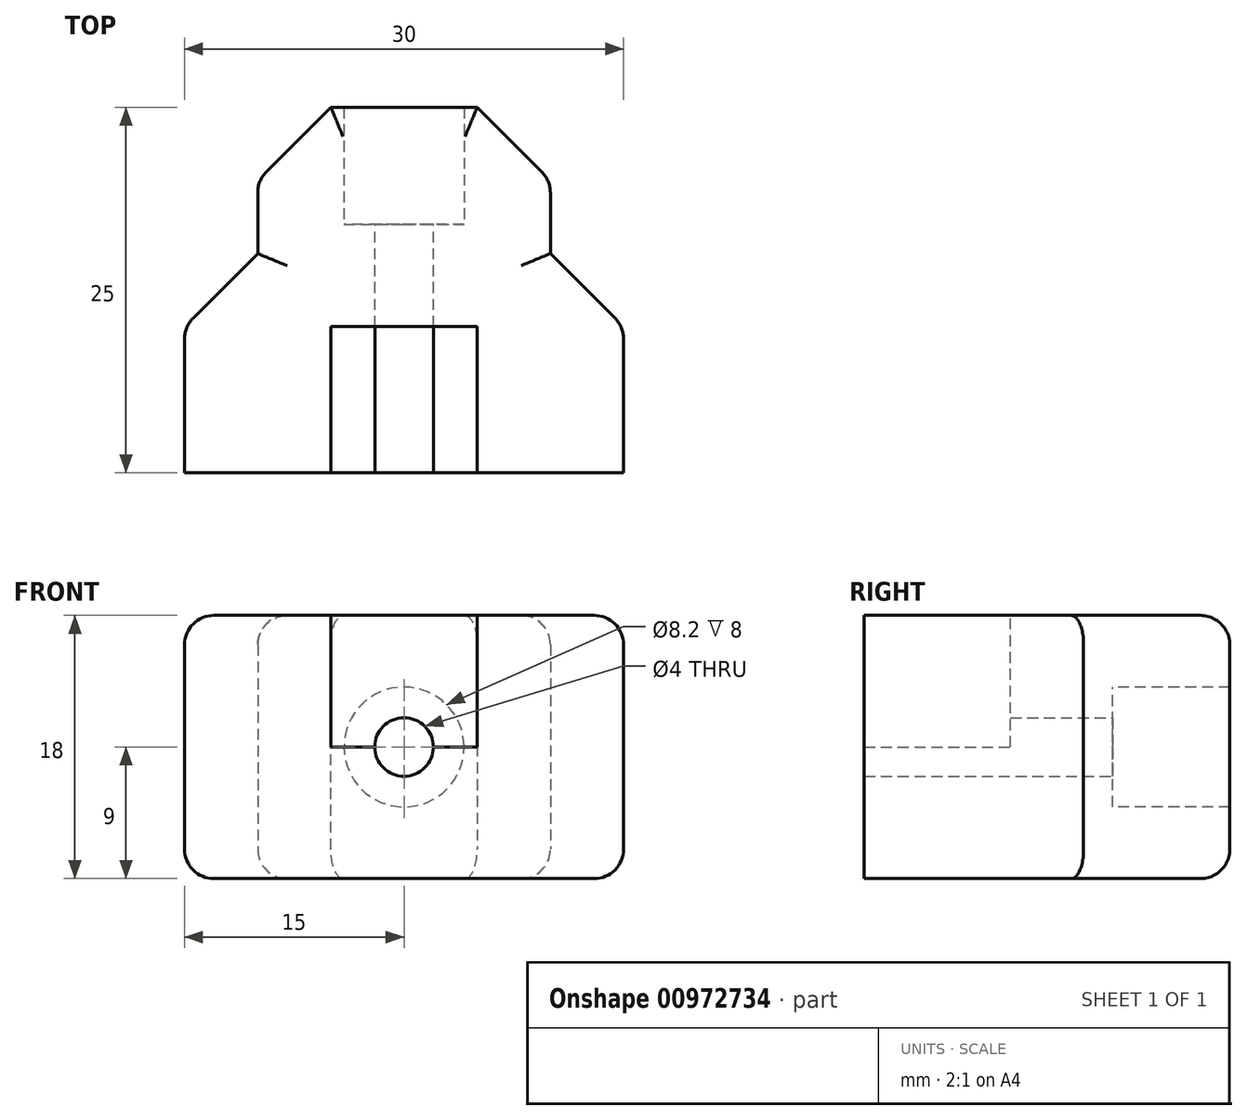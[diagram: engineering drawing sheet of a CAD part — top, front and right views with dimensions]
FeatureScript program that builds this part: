
annotation { "Feature Type Name" : "Feature", "Feature Type Description" : "" }
export const myFeature = defineFeature(function(context is Context, id is Id, definition is map)
    precondition{}
    {
        {
            var Q0;
            Q0=qCreatedBy(makeId("Front.planeOp"),FACE);
            var sketch = newSketch(context, id + "F0", { "sketchPlane" : qUnion([Q0])});
            skLineSegment(sketch, "E0.bottom", {"start": v(15, 9) * mm, "end": v(-15, 9) * mm});
            skLineSegment(sketch, "E0.top", {"start": v(15, -9) * mm, "end": v(-15, -9) * mm});
            skLineSegment(sketch, "E0.left", {"start": v(15, 9) * mm, "end": v(15, -9) * mm});
            skLineSegment(sketch, "E0.right", {"start": v(-15, 9) * mm, "end": v(-15, -9) * mm});
            skPoint(sketch, "E0.middle", {"position": v(0, 0) * mm});
            skLineSegment(sketch, "E1.bottom", {"start": v(10, 9) * mm, "end": v(-10, 9) * mm});
            skLineSegment(sketch, "E1.top", {"start": v(10, -9) * mm, "end": v(-10, -9) * mm});
            skLineSegment(sketch, "E1.left", {"start": v(10, 9) * mm, "end": v(10, -9) * mm});
            skLineSegment(sketch, "E1.right", {"start": v(-10, 9) * mm, "end": v(-10, -9) * mm});
            skCircle(sketch, "E2", {"center": v(0, 0) * mm, "radius": 4.1 * mm});
            skCircle(sketch, "E3", {"center": v(0, 0) * mm, "radius": 2 * mm});
            skLineSegment(sketch, "E4.bottom", {"start": v(-5, 0) * mm, "end": v(5, 0) * mm});
            skLineSegment(sketch, "E4.top", {"start": v(-5, 9) * mm, "end": v(5, 9) * mm});
            skLineSegment(sketch, "E4.left", {"start": v(-5, 0) * mm, "end": v(-5, 9) * mm});
            skLineSegment(sketch, "E4.right", {"start": v(5, 0) * mm, "end": v(5, 9) * mm});
            skSolve(sketch);
        }
        {
            var Q0;
            {var subQ0=sQuery(id+"F0.wireOp",EDGE,"E0.right");Q0=makeQuery(id+"F0.imprint","IMPRINT",FACE,{"disambiguationData":[TD([[makeQuery(id+"F0.imprint","IMPRINT",EDGE,{"derivedFrom":subQ0}),1.0]])]});}
            var Q1;
            {var subQ0=sQuery(id+"F0.wireOp",EDGE,"E1.left");Q1=makeQuery(id+"F0.imprint","IMPRINT",FACE,{"disambiguationData":[TD([[makeQuery(id+"F0.imprint","IMPRINT",EDGE,{"derivedFrom":subQ0}),-1.0]])]});}
            var Q2;
            {var subQ2=sQuery(id+"F0.wireOp",EDGE,"E0.left");Q2=makeQuery(id+"F0.imprint","IMPRINT",FACE,{"disambiguationData":[TD([[makeQuery(id+"F0.imprint","IMPRINT",EDGE,{"derivedFrom":subQ2}),-1.0]])]});}
            var Q3;
            {var subQ0=sQuery(id+"F0.wireOp",EDGE,"E4.bottom");var subQ1=sQuery(id+"F0.wireOp",EDGE,"E2");var subQ2=makeQuery(id+"F0.imprint","INTERSECT",VERTEX,{"disambiguationData":[OD(0.0)],"derivedFrom":[subQ1,subQ0]});Q3=makeQuery(id+"F0.imprint","IMPRINT",FACE,{"disambiguationData":[TD([[makeQuery(id+"F0.imprint","IMPRINT",EDGE,{"disambiguationData":[TD([[subQ2,-1.0]])],"derivedFrom":subQ1}),1.0]])]});}
            extrude(context, id + "F1", {"entities" : qUnion([Q0, Q1, Q2, Q3]), "depth" : 15 * mm, "offsetDistance" : 25 * mm});
        }
        {
            var Q0;
            {var subQ5=sQuery(id+"F0.wireOp",EDGE,"E4.left");Q0=makeQuery(id+"F0.imprint","IMPRINT",FACE,{"disambiguationData":[TD([[makeQuery(id+"F0.imprint","IMPRINT",EDGE,{"derivedFrom":subQ5}),-1.0]])]});}
            var Q1;
            {var subQ0=sQuery(id+"F0.wireOp",EDGE,"E4.bottom");var subQ1=sQuery(id+"F0.wireOp",EDGE,"E2");var subQ2=makeQuery(id+"F0.imprint","INTERSECT",VERTEX,{"disambiguationData":[OD(0.0)],"derivedFrom":[subQ1,subQ0]});Q1=makeQuery(id+"F0.imprint","IMPRINT",FACE,{"disambiguationData":[TD([[makeQuery(id+"F0.imprint","IMPRINT",EDGE,{"disambiguationData":[TD([[subQ2,1.0]])],"derivedFrom":subQ1}),1.0]])]});}
            extrude(context, id + "F2", {"entities" : qUnion([Q0, Q1]), "operationType" : NewBodyOperationType.ADD, "depth" : 5 * mm, "offsetDistance" : 25 * mm});
        }
        {
            var Q0;
            {var subQ0=sQuery(id+"F0.wireOp",EDGE,"E1.left");Q0=makeQuery(id+"F0.imprint","IMPRINT",FACE,{"disambiguationData":[TD([[makeQuery(id+"F0.imprint","IMPRINT",EDGE,{"derivedFrom":subQ0}),-1.0]])]});}
            var Q1;
            {var subQ5=sQuery(id+"F0.wireOp",EDGE,"E4.left");Q1=makeQuery(id+"F0.imprint","IMPRINT",FACE,{"disambiguationData":[TD([[makeQuery(id+"F0.imprint","IMPRINT",EDGE,{"derivedFrom":subQ5}),-1.0]])]});}
            extrude(context, id + "F3", {"entities" : qUnion([Q0, Q1]), "operationType" : NewBodyOperationType.ADD, "oppositeDirection" : true, "depth" : 10 * mm, "offsetDistance" : 25 * mm});
        }
        {
            var Q0;
            {var subQ0=sQuery(id+"F0.wireOp",EDGE,"E4.bottom");var subQ1=sQuery(id+"F0.wireOp",EDGE,"E2");var subQ2=makeQuery(id+"F0.imprint","INTERSECT",VERTEX,{"disambiguationData":[OD(0.0)],"derivedFrom":[subQ1,subQ0]});Q0=makeQuery(id+"F0.imprint","IMPRINT",FACE,{"disambiguationData":[TD([[makeQuery(id+"F0.imprint","IMPRINT",EDGE,{"disambiguationData":[TD([[subQ2,-1.0]])],"derivedFrom":subQ1}),1.0]])]});}
            var Q1;
            {var subQ0=sQuery(id+"F0.wireOp",EDGE,"E4.bottom");var subQ1=sQuery(id+"F0.wireOp",EDGE,"E2");var subQ2=makeQuery(id+"F0.imprint","INTERSECT",VERTEX,{"disambiguationData":[OD(0.0)],"derivedFrom":[subQ1,subQ0]});Q1=makeQuery(id+"F0.imprint","IMPRINT",FACE,{"disambiguationData":[TD([[makeQuery(id+"F0.imprint","IMPRINT",EDGE,{"disambiguationData":[TD([[subQ2,1.0]])],"derivedFrom":subQ1}),1.0]])]});}
            extrude(context, id + "F4", {"entities" : qUnion([Q0, Q1]), "operationType" : NewBodyOperationType.ADD, "oppositeDirection" : true, "depth" : 2 * mm, "offsetDistance" : 25 * mm});
        }
        {
            var Q0;
            Q0=makeQuery(id+"F1.opExtrude","CAP_EDGE",EDGE,{"disambiguationData":[OSD([sQuery(id+"F0.wireOp",EDGE,"E0.right")])],"isStart":true});
            var Q1;
            Q1=makeQuery(id+"F1.opExtrude","CAP_EDGE",EDGE,{"disambiguationData":[OSD([sQuery(id+"F0.wireOp",EDGE,"E0.left")])],"isStart":true});
            var Q2;
            Q2=makeQuery(id+"F3.opExtrude","CAP_EDGE",EDGE,{"disambiguationData":[OSD([sQuery(id+"F0.wireOp",EDGE,"E1.right")])],"isStart":false});
            var Q3;
            Q3=makeQuery(id+"F3.opExtrude","CAP_EDGE",EDGE,{"disambiguationData":[OSD([sQuery(id+"F0.wireOp",EDGE,"E1.left")])],"isStart":false});
            chamfer(context, id + "F5", {"entities" : qUnion([Q0, Q1, Q2, Q3]), "width" : 5 * mm, "tangentPropagation" : true});
        }
        {
            var Q0;
            Q0=makeQuery(id+"F1.opExtrude","SWEPT_EDGE",EDGE,{"disambiguationData":[OSD([sQuery(id+"F0.wireOp",EDGE,"E0.bottom"),sQuery(id+"F0.wireOp",EDGE,"E0.right")])]});
            var Q1;
            {var subQ0=sQuery(id+"F0.wireOp",EDGE,"E0.right");Q1=makeQuery(id+"F5.opChamfer","BLEND_EDGE",EDGE,{"blendedFrom":[makeQuery(id+"F1.opExtrude","CAP_EDGE",EDGE,{"disambiguationData":[OSD([subQ0])],"isStart":true}),makeQuery(id+"F1.opExtrude","SWEPT_FACE",FACE,{"disambiguationData":[OSD([subQ0])]})],"blendedInto":[makeQuery(id+"F1.opExtrude","SWEPT_FACE",FACE,{"disambiguationData":[OSD([subQ0])]})]});}
            var Q2;
            {var subQ0=sQuery(id+"F0.wireOp",EDGE,"E0.bottom");var subQ1=makeQuery(id+"F0.imprint","INTERSECT",VERTEX,{"derivedFrom":[subQ0,sQuery(id+"F0.wireOp",EDGE,"E1.left")]});var subQ2=makeQuery(id+"F0.imprint","INTERSECT",VERTEX,{"derivedFrom":[subQ0,sQuery(id+"F0.wireOp",EDGE,"E1.right")]});var subQ3=sQuery(id+"F0.wireOp",EDGE,"E0.right");Q2=makeQuery(id+"F5.opChamfer","BLEND_EDGE",EDGE,{"blendedFrom":[makeQuery(id+"F1.opExtrude","CAP_EDGE",EDGE,{"disambiguationData":[OSD([subQ3])],"isStart":true}),makeQuery(id+"F3.boolean.opBoolean","MERGE",FACE,{"derivedFrom":[makeQuery(id+"F2.boolean.opBoolean","MERGE",FACE,{"derivedFrom":[makeQuery(id+"F1.opExtrude","SWEPT_FACE",FACE,{"disambiguationData":[OSD([subQ0]),TDD([makeQuery(id+"F0.imprint","IMPRINT",EDGE,{"disambiguationData":[TD([[makeQuery(id+"F0.imprint","INTERSECT",VERTEX,{"derivedFrom":[subQ0,subQ3]}),1.0]])],"derivedFrom":subQ0}),makeQuery(id+"F0.imprint","IMPRINT",EDGE,{"disambiguationData":[TD([[subQ2,1.0]])],"derivedFrom":subQ0})])]}),makeQuery(id+"F1.opExtrude","SWEPT_FACE",FACE,{"disambiguationData":[OSD([subQ0]),TDD([makeQuery(id+"F0.imprint","IMPRINT",EDGE,{"disambiguationData":[TD([[makeQuery(id+"F0.imprint","INTERSECT",VERTEX,{"derivedFrom":[subQ0,sQuery(id+"F0.wireOp",EDGE,"E4.right")]}),1.0]])],"derivedFrom":subQ0}),makeQuery(id+"F0.imprint","IMPRINT",EDGE,{"disambiguationData":[TD([[subQ1,1.0]])],"derivedFrom":subQ0})])]}),makeQuery(id+"F2.opExtrude","SWEPT_FACE",FACE,{"disambiguationData":[OSD([subQ0])]})]}),makeQuery(id+"F3.opExtrude","SWEPT_FACE",FACE,{"disambiguationData":[OSD([subQ0])]})]})],"blendedInto":[makeQuery(id+"F3.boolean.opBoolean","MERGE",FACE,{"derivedFrom":[makeQuery(id+"F2.boolean.opBoolean","MERGE",FACE,{"derivedFrom":[makeQuery(id+"F1.opExtrude","SWEPT_FACE",FACE,{"disambiguationData":[OSD([subQ0]),TDD([makeQuery(id+"F0.imprint","IMPRINT",EDGE,{"disambiguationData":[TD([[makeQuery(id+"F0.imprint","INTERSECT",VERTEX,{"derivedFrom":[subQ0,subQ3]}),1.0]])],"derivedFrom":subQ0}),makeQuery(id+"F0.imprint","IMPRINT",EDGE,{"disambiguationData":[TD([[subQ2,1.0]])],"derivedFrom":subQ0})])]}),makeQuery(id+"F1.opExtrude","SWEPT_FACE",FACE,{"disambiguationData":[OSD([subQ0]),TDD([makeQuery(id+"F0.imprint","IMPRINT",EDGE,{"disambiguationData":[TD([[makeQuery(id+"F0.imprint","INTERSECT",VERTEX,{"derivedFrom":[subQ0,sQuery(id+"F0.wireOp",EDGE,"E4.right")]}),1.0]])],"derivedFrom":subQ0}),makeQuery(id+"F0.imprint","IMPRINT",EDGE,{"disambiguationData":[TD([[subQ1,1.0]])],"derivedFrom":subQ0})])]}),makeQuery(id+"F2.opExtrude","SWEPT_FACE",FACE,{"disambiguationData":[OSD([subQ0])]})]}),makeQuery(id+"F3.opExtrude","SWEPT_FACE",FACE,{"disambiguationData":[OSD([subQ0])]})]})]});}
            var Q3;
            Q3=makeQuery(id+"F3.opExtrude","SWEPT_EDGE",EDGE,{"disambiguationData":[OSD([sQuery(id+"F0.wireOp",EDGE,"E0.bottom"),sQuery(id+"F0.wireOp",EDGE,"E1.right")])]});
            var Q4;
            {var subQ0=sQuery(id+"F0.wireOp",EDGE,"E1.right");Q4=makeQuery(id+"F5.opChamfer","BLEND_EDGE",EDGE,{"blendedFrom":[makeQuery(id+"F3.opExtrude","CAP_EDGE",EDGE,{"disambiguationData":[OSD([subQ0])],"isStart":false}),makeQuery(id+"F3.opExtrude","SWEPT_FACE",FACE,{"disambiguationData":[OSD([subQ0])]})],"blendedInto":[makeQuery(id+"F3.opExtrude","SWEPT_FACE",FACE,{"disambiguationData":[OSD([subQ0])]})]});}
            var Q5;
            {var subQ0=sQuery(id+"F0.wireOp",EDGE,"E0.bottom");var subQ1=makeQuery(id+"F0.imprint","INTERSECT",VERTEX,{"derivedFrom":[subQ0,sQuery(id+"F0.wireOp",EDGE,"E1.left")]});var subQ2=sQuery(id+"F0.wireOp",EDGE,"E1.right");var subQ3=makeQuery(id+"F0.imprint","INTERSECT",VERTEX,{"derivedFrom":[subQ0,subQ2]});Q5=makeQuery(id+"F5.opChamfer","BLEND_EDGE",EDGE,{"blendedFrom":[makeQuery(id+"F3.opExtrude","CAP_EDGE",EDGE,{"disambiguationData":[OSD([subQ2])],"isStart":false}),makeQuery(id+"F3.boolean.opBoolean","MERGE",FACE,{"derivedFrom":[makeQuery(id+"F2.boolean.opBoolean","MERGE",FACE,{"derivedFrom":[makeQuery(id+"F1.opExtrude","SWEPT_FACE",FACE,{"disambiguationData":[OSD([subQ0]),TDD([makeQuery(id+"F0.imprint","IMPRINT",EDGE,{"disambiguationData":[TD([[makeQuery(id+"F0.imprint","INTERSECT",VERTEX,{"derivedFrom":[subQ0,sQuery(id+"F0.wireOp",EDGE,"E0.right")]}),1.0]])],"derivedFrom":subQ0}),makeQuery(id+"F0.imprint","IMPRINT",EDGE,{"disambiguationData":[TD([[subQ3,1.0]])],"derivedFrom":subQ0})])]}),makeQuery(id+"F1.opExtrude","SWEPT_FACE",FACE,{"disambiguationData":[OSD([subQ0]),TDD([makeQuery(id+"F0.imprint","IMPRINT",EDGE,{"disambiguationData":[TD([[makeQuery(id+"F0.imprint","INTERSECT",VERTEX,{"derivedFrom":[subQ0,sQuery(id+"F0.wireOp",EDGE,"E4.right")]}),1.0]])],"derivedFrom":subQ0}),makeQuery(id+"F0.imprint","IMPRINT",EDGE,{"disambiguationData":[TD([[subQ1,1.0]])],"derivedFrom":subQ0})])]}),makeQuery(id+"F2.opExtrude","SWEPT_FACE",FACE,{"disambiguationData":[OSD([subQ0])]})]}),makeQuery(id+"F3.opExtrude","SWEPT_FACE",FACE,{"disambiguationData":[OSD([subQ0])]})]})],"blendedInto":[makeQuery(id+"F3.boolean.opBoolean","MERGE",FACE,{"derivedFrom":[makeQuery(id+"F2.boolean.opBoolean","MERGE",FACE,{"derivedFrom":[makeQuery(id+"F1.opExtrude","SWEPT_FACE",FACE,{"disambiguationData":[OSD([subQ0]),TDD([makeQuery(id+"F0.imprint","IMPRINT",EDGE,{"disambiguationData":[TD([[makeQuery(id+"F0.imprint","INTERSECT",VERTEX,{"derivedFrom":[subQ0,sQuery(id+"F0.wireOp",EDGE,"E0.right")]}),1.0]])],"derivedFrom":subQ0}),makeQuery(id+"F0.imprint","IMPRINT",EDGE,{"disambiguationData":[TD([[subQ3,1.0]])],"derivedFrom":subQ0})])]}),makeQuery(id+"F1.opExtrude","SWEPT_FACE",FACE,{"disambiguationData":[OSD([subQ0]),TDD([makeQuery(id+"F0.imprint","IMPRINT",EDGE,{"disambiguationData":[TD([[makeQuery(id+"F0.imprint","INTERSECT",VERTEX,{"derivedFrom":[subQ0,sQuery(id+"F0.wireOp",EDGE,"E4.right")]}),1.0]])],"derivedFrom":subQ0}),makeQuery(id+"F0.imprint","IMPRINT",EDGE,{"disambiguationData":[TD([[subQ1,1.0]])],"derivedFrom":subQ0})])]}),makeQuery(id+"F2.opExtrude","SWEPT_FACE",FACE,{"disambiguationData":[OSD([subQ0])]})]}),makeQuery(id+"F3.opExtrude","SWEPT_FACE",FACE,{"disambiguationData":[OSD([subQ0])]})]})]});}
            var Q6;
            {var subQ0=sQuery(id+"F0.wireOp",EDGE,"E0.bottom");var subQ1=sQuery(id+"F0.wireOp",EDGE,"E1.left");var subQ2=makeQuery(id+"F0.imprint","INTERSECT",VERTEX,{"derivedFrom":[subQ0,subQ1]});var subQ3=makeQuery(id+"F0.imprint","INTERSECT",VERTEX,{"derivedFrom":[subQ0,sQuery(id+"F0.wireOp",EDGE,"E1.right")]});Q6=makeQuery(id+"F5.opChamfer","BLEND_EDGE",EDGE,{"blendedFrom":[makeQuery(id+"F3.opExtrude","CAP_EDGE",EDGE,{"disambiguationData":[OSD([subQ1])],"isStart":false}),makeQuery(id+"F3.boolean.opBoolean","MERGE",FACE,{"derivedFrom":[makeQuery(id+"F2.boolean.opBoolean","MERGE",FACE,{"derivedFrom":[makeQuery(id+"F1.opExtrude","SWEPT_FACE",FACE,{"disambiguationData":[OSD([subQ0]),TDD([makeQuery(id+"F0.imprint","IMPRINT",EDGE,{"disambiguationData":[TD([[makeQuery(id+"F0.imprint","INTERSECT",VERTEX,{"derivedFrom":[subQ0,sQuery(id+"F0.wireOp",EDGE,"E0.right")]}),1.0]])],"derivedFrom":subQ0}),makeQuery(id+"F0.imprint","IMPRINT",EDGE,{"disambiguationData":[TD([[subQ3,1.0]])],"derivedFrom":subQ0})])]}),makeQuery(id+"F1.opExtrude","SWEPT_FACE",FACE,{"disambiguationData":[OSD([subQ0]),TDD([makeQuery(id+"F0.imprint","IMPRINT",EDGE,{"disambiguationData":[TD([[makeQuery(id+"F0.imprint","INTERSECT",VERTEX,{"derivedFrom":[subQ0,sQuery(id+"F0.wireOp",EDGE,"E4.right")]}),1.0]])],"derivedFrom":subQ0}),makeQuery(id+"F0.imprint","IMPRINT",EDGE,{"disambiguationData":[TD([[subQ2,1.0]])],"derivedFrom":subQ0})])]}),makeQuery(id+"F2.opExtrude","SWEPT_FACE",FACE,{"disambiguationData":[OSD([subQ0])]})]}),makeQuery(id+"F3.opExtrude","SWEPT_FACE",FACE,{"disambiguationData":[OSD([subQ0])]})]})],"blendedInto":[makeQuery(id+"F3.boolean.opBoolean","MERGE",FACE,{"derivedFrom":[makeQuery(id+"F2.boolean.opBoolean","MERGE",FACE,{"derivedFrom":[makeQuery(id+"F1.opExtrude","SWEPT_FACE",FACE,{"disambiguationData":[OSD([subQ0]),TDD([makeQuery(id+"F0.imprint","IMPRINT",EDGE,{"disambiguationData":[TD([[makeQuery(id+"F0.imprint","INTERSECT",VERTEX,{"derivedFrom":[subQ0,sQuery(id+"F0.wireOp",EDGE,"E0.right")]}),1.0]])],"derivedFrom":subQ0}),makeQuery(id+"F0.imprint","IMPRINT",EDGE,{"disambiguationData":[TD([[subQ3,1.0]])],"derivedFrom":subQ0})])]}),makeQuery(id+"F1.opExtrude","SWEPT_FACE",FACE,{"disambiguationData":[OSD([subQ0]),TDD([makeQuery(id+"F0.imprint","IMPRINT",EDGE,{"disambiguationData":[TD([[makeQuery(id+"F0.imprint","INTERSECT",VERTEX,{"derivedFrom":[subQ0,sQuery(id+"F0.wireOp",EDGE,"E4.right")]}),1.0]])],"derivedFrom":subQ0}),makeQuery(id+"F0.imprint","IMPRINT",EDGE,{"disambiguationData":[TD([[subQ2,1.0]])],"derivedFrom":subQ0})])]}),makeQuery(id+"F2.opExtrude","SWEPT_FACE",FACE,{"disambiguationData":[OSD([subQ0])]})]}),makeQuery(id+"F3.opExtrude","SWEPT_FACE",FACE,{"disambiguationData":[OSD([subQ0])]})]})]});}
            var Q7;
            Q7=makeQuery(id+"F3.opExtrude","CAP_EDGE",EDGE,{"disambiguationData":[OSD([sQuery(id+"F0.wireOp",EDGE,"E0.bottom")])],"isStart":false});
            var Q8;
            Q8=makeQuery(id+"F3.opExtrude","SWEPT_EDGE",EDGE,{"disambiguationData":[OSD([sQuery(id+"F0.wireOp",EDGE,"E0.bottom"),sQuery(id+"F0.wireOp",EDGE,"E1.left")])]});
            var Q9;
            {var subQ0=sQuery(id+"F0.wireOp",EDGE,"E0.bottom");var subQ1=makeQuery(id+"F0.imprint","INTERSECT",VERTEX,{"derivedFrom":[subQ0,sQuery(id+"F0.wireOp",EDGE,"E1.left")]});var subQ2=sQuery(id+"F0.wireOp",EDGE,"E0.left");var subQ3=makeQuery(id+"F0.imprint","INTERSECT",VERTEX,{"derivedFrom":[subQ0,sQuery(id+"F0.wireOp",EDGE,"E1.right")]});Q9=makeQuery(id+"F5.opChamfer","BLEND_EDGE",EDGE,{"blendedFrom":[makeQuery(id+"F1.opExtrude","CAP_EDGE",EDGE,{"disambiguationData":[OSD([subQ2])],"isStart":true}),makeQuery(id+"F3.boolean.opBoolean","MERGE",FACE,{"derivedFrom":[makeQuery(id+"F2.boolean.opBoolean","MERGE",FACE,{"derivedFrom":[makeQuery(id+"F1.opExtrude","SWEPT_FACE",FACE,{"disambiguationData":[OSD([subQ0]),TDD([makeQuery(id+"F0.imprint","IMPRINT",EDGE,{"disambiguationData":[TD([[makeQuery(id+"F0.imprint","INTERSECT",VERTEX,{"derivedFrom":[subQ0,sQuery(id+"F0.wireOp",EDGE,"E0.right")]}),1.0]])],"derivedFrom":subQ0}),makeQuery(id+"F0.imprint","IMPRINT",EDGE,{"disambiguationData":[TD([[subQ3,1.0]])],"derivedFrom":subQ0})])]}),makeQuery(id+"F1.opExtrude","SWEPT_FACE",FACE,{"disambiguationData":[OSD([subQ0]),TDD([makeQuery(id+"F0.imprint","IMPRINT",EDGE,{"disambiguationData":[TD([[makeQuery(id+"F0.imprint","INTERSECT",VERTEX,{"derivedFrom":[subQ0,sQuery(id+"F0.wireOp",EDGE,"E4.right")]}),1.0]])],"derivedFrom":subQ0}),makeQuery(id+"F0.imprint","IMPRINT",EDGE,{"disambiguationData":[TD([[subQ1,1.0]])],"derivedFrom":subQ0})])]}),makeQuery(id+"F2.opExtrude","SWEPT_FACE",FACE,{"disambiguationData":[OSD([subQ0])]})]}),makeQuery(id+"F3.opExtrude","SWEPT_FACE",FACE,{"disambiguationData":[OSD([subQ0])]})]})],"blendedInto":[makeQuery(id+"F3.boolean.opBoolean","MERGE",FACE,{"derivedFrom":[makeQuery(id+"F2.boolean.opBoolean","MERGE",FACE,{"derivedFrom":[makeQuery(id+"F1.opExtrude","SWEPT_FACE",FACE,{"disambiguationData":[OSD([subQ0]),TDD([makeQuery(id+"F0.imprint","IMPRINT",EDGE,{"disambiguationData":[TD([[makeQuery(id+"F0.imprint","INTERSECT",VERTEX,{"derivedFrom":[subQ0,sQuery(id+"F0.wireOp",EDGE,"E0.right")]}),1.0]])],"derivedFrom":subQ0}),makeQuery(id+"F0.imprint","IMPRINT",EDGE,{"disambiguationData":[TD([[subQ3,1.0]])],"derivedFrom":subQ0})])]}),makeQuery(id+"F1.opExtrude","SWEPT_FACE",FACE,{"disambiguationData":[OSD([subQ0]),TDD([makeQuery(id+"F0.imprint","IMPRINT",EDGE,{"disambiguationData":[TD([[makeQuery(id+"F0.imprint","INTERSECT",VERTEX,{"derivedFrom":[subQ0,sQuery(id+"F0.wireOp",EDGE,"E4.right")]}),1.0]])],"derivedFrom":subQ0}),makeQuery(id+"F0.imprint","IMPRINT",EDGE,{"disambiguationData":[TD([[subQ1,1.0]])],"derivedFrom":subQ0})])]}),makeQuery(id+"F2.opExtrude","SWEPT_FACE",FACE,{"disambiguationData":[OSD([subQ0])]})]}),makeQuery(id+"F3.opExtrude","SWEPT_FACE",FACE,{"disambiguationData":[OSD([subQ0])]})]})]});}
            var Q10;
            Q10=makeQuery(id+"F1.opExtrude","SWEPT_EDGE",EDGE,{"disambiguationData":[OSD([sQuery(id+"F0.wireOp",EDGE,"E0.bottom"),sQuery(id+"F0.wireOp",EDGE,"E0.left")])]});
            var Q11;
            Q11=makeQuery(id+"F3.opExtrude","CAP_EDGE",EDGE,{"disambiguationData":[OSD([sQuery(id+"F0.wireOp",EDGE,"E0.top")])],"isStart":false});
            var Q12;
            {var subQ0=sQuery(id+"F0.wireOp",EDGE,"E0.top");Q12=makeQuery(id+"F5.opChamfer","BLEND_EDGE",EDGE,{"blendedFrom":[makeQuery(id+"F3.opExtrude","CAP_EDGE",EDGE,{"disambiguationData":[OSD([sQuery(id+"F0.wireOp",EDGE,"E1.left")])],"isStart":false}),makeQuery(id+"F3.boolean.opBoolean","MERGE",FACE,{"derivedFrom":[makeQuery(id+"F1.opExtrude","SWEPT_FACE",FACE,{"disambiguationData":[OSD([subQ0])]}),makeQuery(id+"F3.opExtrude","SWEPT_FACE",FACE,{"disambiguationData":[OSD([subQ0])]})]})],"blendedInto":[makeQuery(id+"F3.boolean.opBoolean","MERGE",FACE,{"derivedFrom":[makeQuery(id+"F1.opExtrude","SWEPT_FACE",FACE,{"disambiguationData":[OSD([subQ0])]}),makeQuery(id+"F3.opExtrude","SWEPT_FACE",FACE,{"disambiguationData":[OSD([subQ0])]})]})]});}
            var Q13;
            Q13=makeQuery(id+"F3.opExtrude","SWEPT_EDGE",EDGE,{"disambiguationData":[OSD([sQuery(id+"F0.wireOp",EDGE,"E0.top"),sQuery(id+"F0.wireOp",EDGE,"E1.left")])]});
            var Q14;
            {var subQ0=sQuery(id+"F0.wireOp",EDGE,"E0.top");Q14=makeQuery(id+"F5.opChamfer","BLEND_EDGE",EDGE,{"blendedFrom":[makeQuery(id+"F1.opExtrude","CAP_EDGE",EDGE,{"disambiguationData":[OSD([sQuery(id+"F0.wireOp",EDGE,"E0.left")])],"isStart":true}),makeQuery(id+"F3.boolean.opBoolean","MERGE",FACE,{"derivedFrom":[makeQuery(id+"F1.opExtrude","SWEPT_FACE",FACE,{"disambiguationData":[OSD([subQ0])]}),makeQuery(id+"F3.opExtrude","SWEPT_FACE",FACE,{"disambiguationData":[OSD([subQ0])]})]})],"blendedInto":[makeQuery(id+"F3.boolean.opBoolean","MERGE",FACE,{"derivedFrom":[makeQuery(id+"F1.opExtrude","SWEPT_FACE",FACE,{"disambiguationData":[OSD([subQ0])]}),makeQuery(id+"F3.opExtrude","SWEPT_FACE",FACE,{"disambiguationData":[OSD([subQ0])]})]})]});}
            var Q15;
            Q15=makeQuery(id+"F1.opExtrude","SWEPT_EDGE",EDGE,{"disambiguationData":[OSD([sQuery(id+"F0.wireOp",EDGE,"E0.top"),sQuery(id+"F0.wireOp",EDGE,"E0.left")])]});
            var Q16;
            {var subQ0=sQuery(id+"F0.wireOp",EDGE,"E0.top");Q16=makeQuery(id+"F5.opChamfer","BLEND_EDGE",EDGE,{"blendedFrom":[makeQuery(id+"F3.opExtrude","CAP_EDGE",EDGE,{"disambiguationData":[OSD([sQuery(id+"F0.wireOp",EDGE,"E1.right")])],"isStart":false}),makeQuery(id+"F3.boolean.opBoolean","MERGE",FACE,{"derivedFrom":[makeQuery(id+"F1.opExtrude","SWEPT_FACE",FACE,{"disambiguationData":[OSD([subQ0])]}),makeQuery(id+"F3.opExtrude","SWEPT_FACE",FACE,{"disambiguationData":[OSD([subQ0])]})]})],"blendedInto":[makeQuery(id+"F3.boolean.opBoolean","MERGE",FACE,{"derivedFrom":[makeQuery(id+"F1.opExtrude","SWEPT_FACE",FACE,{"disambiguationData":[OSD([subQ0])]}),makeQuery(id+"F3.opExtrude","SWEPT_FACE",FACE,{"disambiguationData":[OSD([subQ0])]})]})]});}
            var Q17;
            Q17=makeQuery(id+"F3.opExtrude","SWEPT_EDGE",EDGE,{"disambiguationData":[OSD([sQuery(id+"F0.wireOp",EDGE,"E0.top"),sQuery(id+"F0.wireOp",EDGE,"E1.right")])]});
            var Q18;
            {var subQ0=sQuery(id+"F0.wireOp",EDGE,"E0.top");Q18=makeQuery(id+"F5.opChamfer","BLEND_EDGE",EDGE,{"blendedFrom":[makeQuery(id+"F1.opExtrude","CAP_EDGE",EDGE,{"disambiguationData":[OSD([sQuery(id+"F0.wireOp",EDGE,"E0.right")])],"isStart":true}),makeQuery(id+"F3.boolean.opBoolean","MERGE",FACE,{"derivedFrom":[makeQuery(id+"F1.opExtrude","SWEPT_FACE",FACE,{"disambiguationData":[OSD([subQ0])]}),makeQuery(id+"F3.opExtrude","SWEPT_FACE",FACE,{"disambiguationData":[OSD([subQ0])]})]})],"blendedInto":[makeQuery(id+"F3.boolean.opBoolean","MERGE",FACE,{"derivedFrom":[makeQuery(id+"F1.opExtrude","SWEPT_FACE",FACE,{"disambiguationData":[OSD([subQ0])]}),makeQuery(id+"F3.opExtrude","SWEPT_FACE",FACE,{"disambiguationData":[OSD([subQ0])]})]})]});}
            var Q19;
            Q19=makeQuery(id+"F1.opExtrude","SWEPT_EDGE",EDGE,{"disambiguationData":[OSD([sQuery(id+"F0.wireOp",EDGE,"E0.top"),sQuery(id+"F0.wireOp",EDGE,"E0.right")])]});
            var Q20;
            {var subQ0=sQuery(id+"F0.wireOp",EDGE,"E1.left");Q20=makeQuery(id+"F5.opChamfer","BLEND_EDGE",EDGE,{"blendedFrom":[makeQuery(id+"F3.opExtrude","CAP_EDGE",EDGE,{"disambiguationData":[OSD([subQ0])],"isStart":false}),makeQuery(id+"F3.opExtrude","SWEPT_FACE",FACE,{"disambiguationData":[OSD([subQ0])]})],"blendedInto":[makeQuery(id+"F3.opExtrude","SWEPT_FACE",FACE,{"disambiguationData":[OSD([subQ0])]})]});}
            var Q21;
            {var subQ0=sQuery(id+"F0.wireOp",EDGE,"E0.left");Q21=makeQuery(id+"F5.opChamfer","BLEND_EDGE",EDGE,{"blendedFrom":[makeQuery(id+"F1.opExtrude","CAP_EDGE",EDGE,{"disambiguationData":[OSD([subQ0])],"isStart":true}),makeQuery(id+"F1.opExtrude","SWEPT_FACE",FACE,{"disambiguationData":[OSD([subQ0])]})],"blendedInto":[makeQuery(id+"F1.opExtrude","SWEPT_FACE",FACE,{"disambiguationData":[OSD([subQ0])]})]});}
            fillet(context, id + "F6", {"entities" : qUnion([Q0, Q1, Q2, Q3, Q4, Q5, Q6, Q7, Q8, Q9, Q10, Q11, Q12, Q13, Q14, Q15, Q16, Q17, Q18, Q19, Q20, Q21]), "radius" : 2 * mm, "tangentPropagation" : true, "allowEdgeOverflow" : false});
        }
    });
